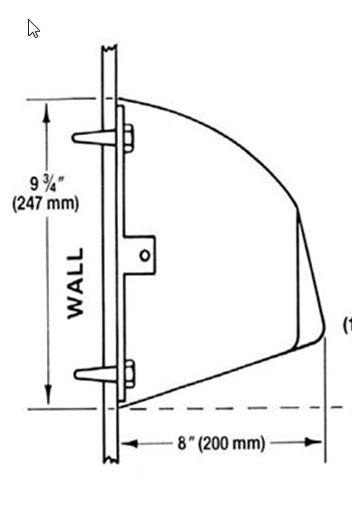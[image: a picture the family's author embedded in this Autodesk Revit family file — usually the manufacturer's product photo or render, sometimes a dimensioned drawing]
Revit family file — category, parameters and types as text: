
# Revit family: Hand-Dryer_Excel_CastCover-ThinAir-Surface
name_source: partatom
category: Electrical Fixtures
units: mm (PartAtom-declared; Revit-internal decimal feet)

## family parameters
Cut with Voids When Loaded = No
Host = Face
Maintain Annotation Orientation = No
Part Type = Normal
Room Calculation Point = No
Round Connector Dimension = Use Diameter
Shared = No

## types (10) — shared parameters
ADA Compliant = Yes
Actuation = 90 seconds lockout for Hands
Air Output = 180 cfm
Air Temperature = 145 F at 72 F ambient room temperature
Assembly Code = C1030210
Automatic = Yes
Building Codes = http://www.ada.gov
Cover Material = Metal - ExcelDryer - Zinc Alloy
Default Elevation = 4' - 0"
Description = Excel Dryer HO-IW Automatic Electric Hand Dryer
Drying Time = 14 Seconds
Green Building-LEED = http://www.arcat.com
Installation-Fabrication = http://www.exceldryer.com
Keynote = 10810
Manual = No
Manufacturer = Excel Dryer
Manufacturer Fax = 413-525-2853
Manufacturer Website = http://www.exceldryer.com
Model = HO-IW
Product Data = http://www.arcat.com
Revision = R1_3_2012
Sales Information = http://www.exceldryer.com
Send Message = http://admin.arcat.com
Specification = http://www.arcat.com
Standards Conformance = UL Listed
URL = http://www.exceldryer.com
Vandal Proof Heater = Yes
zero-valued in all types: Expected Lifespan (Years), Maintenance Schedule (Months), Warranty Duration (Years)

## per-type parameters (varying)
| type | Frequency | MEP Amperage | MEP Wattage | Surface Finish | Unit Weight | Voltage_MEP |
| Excel ThinAir Hand Dryer -  Model TA-ABS - White Polymer (ABS) - 120V - 60Hz | 60 Hz | 8 A | 915 VA | Paint - ExcelDryer - White Polymer | 8 | 120 V |
| Excel ThinAir Hand Dryer -  Model TA-ABS - White Polymer (ABS) - 277V - 60Hz | 60 Hz | 4 A | 950 VA | Paint - ExcelDryer - White Polymer | 8 | 277 V |
| Excel ThinAir Hand Dryer -  Model TA-ABS - White Polymer (ABS) - 230V - 50Hz | 50 Hz | 4 A | 890 VA | Paint - ExcelDryer - White Polymer | 8 | 230 V |
| Excel ThinAir Hand Dryer -  Model TA-SB - Brushed Stainless Steel - 120V - 60Hz | 60 Hz | 8 A | 915 VA | Metal - ExcelDryer - Brushed Stainless Steel | 10 | 120 V |
| Excel ThinAir Hand Dryer -  Model TA-SB - Brushed Stainless Steel - 277V - 60Hz | 60 Hz | 4 A | 950 VA | Metal - ExcelDryer - Brushed Stainless Steel | 10 | 277 V |
| Excel ThinAir Hand Dryer -  Model TA-SB - Brushed Stainless Steel - 230V - 50Hz | 50 Hz | 4 A | 890 VA | Metal - ExcelDryer - Brushed Stainless Steel | 10 | 230 V |
| Excel ThinAir Hand Dryer -  Model TA-ABS - White Polymer (ABS) - 120V - 50Hz | 50 Hz | 8 A | 915 VA | Paint - ExcelDryer - White Polymer | 8 | 120 V |
| Excel ThinAir Hand Dryer -  Model TA-ABS - White Polymer (ABS) - 277V - 50Hz | 50 Hz | 4 A | 950 VA | Paint - ExcelDryer - White Polymer | 8 | 277 V |
| Excel ThinAir Hand Dryer -  Model TA-SB - Brushed Stainless Steel - 120V - 50Hz | 50 Hz | 8 A | 915 VA | Metal - ExcelDryer - Brushed Stainless Steel | 10 | 120 V |
| Excel ThinAir Hand Dryer -  Model TA-SB - Brushed Stainless Steel - 277V - 50Hz | 50 Hz | 4 A | 950 VA | Metal - ExcelDryer - Brushed Stainless Steel | 10 | 277 V |

## geometry (parser evidence)
native form markers: Sweep x3
no freeform markers — native parametric forms only
